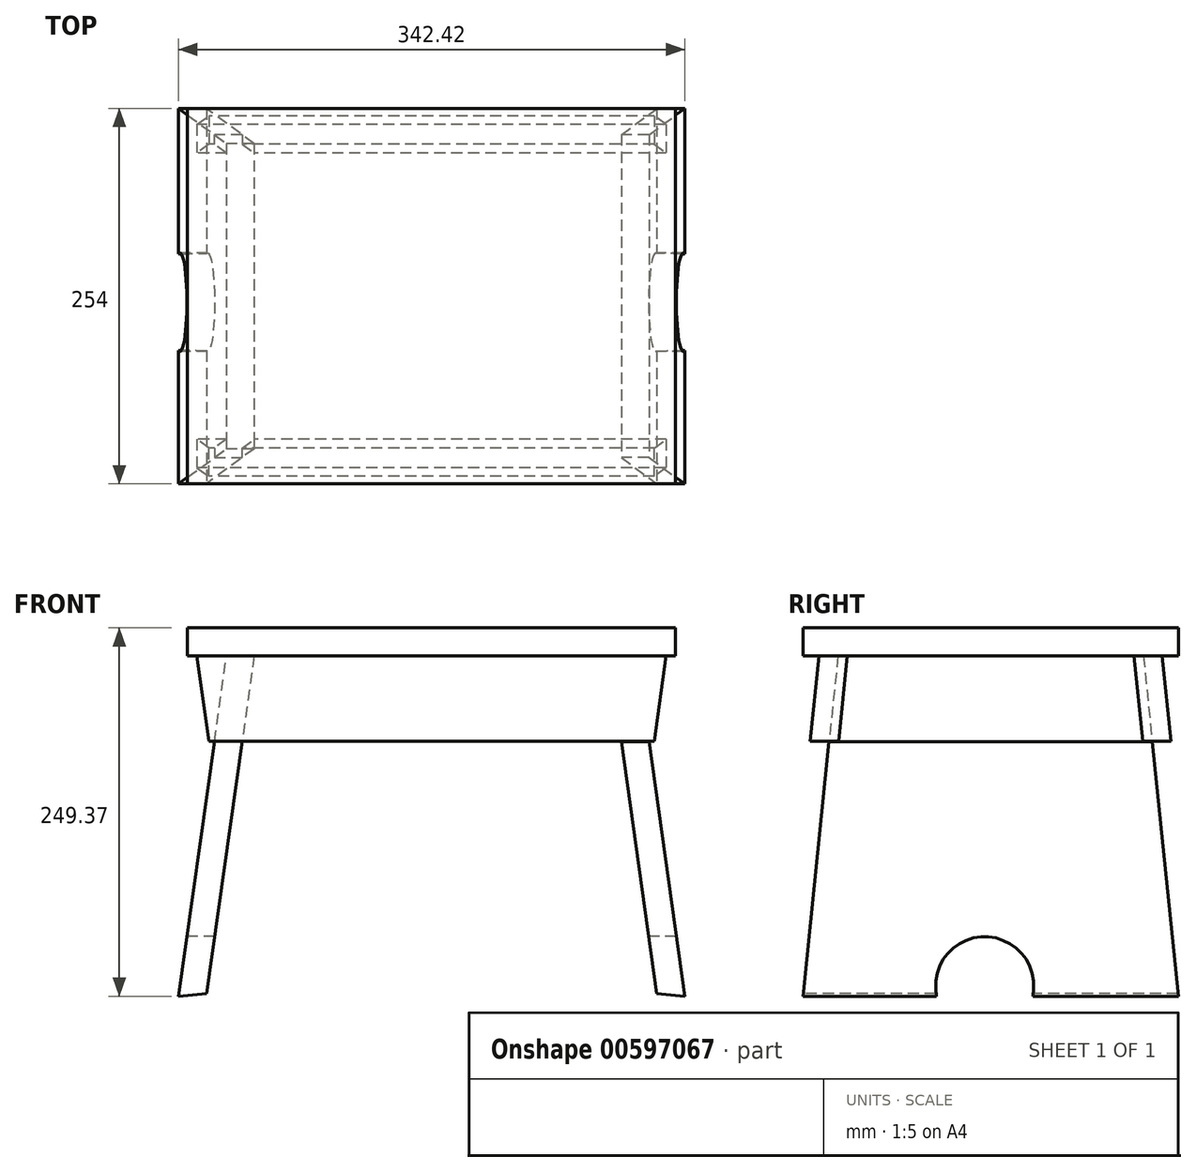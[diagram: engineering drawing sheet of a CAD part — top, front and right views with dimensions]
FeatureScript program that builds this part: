
annotation { "Feature Type Name" : "Feature", "Feature Type Description" : "" }
export const myFeature = defineFeature(function(context is Context, id is Id, definition is map)
    precondition{}
    {
        {
            var Q0;
            Q0=qCreatedBy(makeId("Front.planeOp"),FACE);
            var sketch = newSketch(context, id + "F0", { "sketchPlane" : qUnion([Q0])});
            skLineSegment(sketch, "E0.bottom", {"start": v(165.1, -9.52) * mm, "end": v(-165.1, -9.53) * mm});
            skLineSegment(sketch, "E0.top", {"start": v(165.1, 9.53) * mm, "end": v(-165.1, 9.52) * mm});
            skLineSegment(sketch, "E0.left", {"start": v(165.1, -9.53) * mm, "end": v(165.1, 9.52) * mm});
            skLineSegment(sketch, "E0.right", {"start": v(-165.1, -9.53) * mm, "end": v(-165.1, 9.52) * mm});
            skPoint(sketch, "E0.middle", {"position": v(0, 0) * mm});
            skLineSegment(sketch, "E1.bottom", {"start": v(-165.1, -9.53) * mm, "end": v(165.1, -9.53) * mm, "construction": true});
            skLineSegment(sketch, "E1.top", {"start": v(-165.1, -238.13) * mm, "end": v(165.1, -238.13) * mm, "construction": true});
            skLineSegment(sketch, "E1.left", {"start": v(-165.1, -9.53) * mm, "end": v(-165.1, -238.13) * mm, "construction": true});
            skLineSegment(sketch, "E1.right", {"start": v(165.1, -9.53) * mm, "end": v(165.1, -238.13) * mm, "construction": true});
            skLineSegment(sketch, "E2", {"start": v(171.21, -239.84) * mm, "end": v(152.24, -238.13) * mm});
            skLineSegment(sketch, "E3", {"start": v(0, 0) * mm, "end": v(0, -238.13) * mm, "construction": true});
            skLineSegment(sketch, "E4.MirrorCS", {"start": v(165.1, -9.53) * mm, "end": v(-165.1, -9.53) * mm, "construction": true});
            skLineSegment(sketch, "E5.MirrorCS", {"start": v(-171.21, -239.84) * mm, "end": v(-152.24, -238.13) * mm});
            skLineSegment(sketch, "E6.MirrorCS", {"start": v(-138.85, -9.53) * mm, "end": v(-171.21, -239.84) * mm});
            skLineSegment(sketch, "E7.bottom", {"start": v(-165.1, -9.53) * mm, "end": v(165.1, -9.53) * mm});
            skLineSegment(sketch, "E7.top", {"start": v(-165.1, -67.6) * mm, "end": v(165.1, -67.6) * mm});
            skLineSegment(sketch, "E7.left", {"start": v(-165.1, -9.53) * mm, "end": v(-165.1, -67.6) * mm});
            skLineSegment(sketch, "E7.right", {"start": v(165.1, -9.53) * mm, "end": v(165.1, -67.6) * mm});
            skLineSegment(sketch, "E8", {"start": v(150.59, -67.6) * mm, "end": v(158.75, -9.53) * mm});
            skLineSegment(sketch, "E9.MirrorCS", {"start": v(-150.59, -67.6) * mm, "end": v(-158.75, -9.53) * mm});
            skLineSegment(sketch, "E10", {"start": v(-152.24, -238.13) * mm, "end": v(-120.11, -9.53) * mm});
            skLineSegment(sketch, "E11.MirrorCS", {"start": v(152.24, -238.13) * mm, "end": v(120.11, -9.53) * mm});
            skLineSegment(sketch, "E12.MirrorCS", {"start": v(165.1, -238.13) * mm, "end": v(-165.1, -238.13) * mm, "construction": true});
            skLineSegment(sketch, "E13", {"start": v(171.21, -239.84) * mm, "end": v(138.85, -9.53) * mm});
            skSolve(sketch);
        }
        {
            var Q0;
            Q0=makeQuery(id+"F0.imprint","IMPRINT",FACE,{"disambiguationData":[TD([[makeQuery(id+"F0.imprint","IMPRINT",EDGE,{"derivedFrom":sQuery(id+"F0.wireOp",EDGE,"E0.top")}),1.0]])]});
            extrude(context, id + "F1", {"entities" : qUnion([Q0]), "endBound" : BoundingType.SYMMETRIC, "depth" : 254 * mm, "offsetDistance" : 25.4 * mm});
        }
        {
            var Q0;
            {var subQ0=sQuery(id+"F0.wireOp",EDGE,"E5.MirrorCS");Q0=makeQuery(id+"F0.imprint","IMPRINT",FACE,{"disambiguationData":[TD([[makeQuery(id+"F0.imprint","IMPRINT",EDGE,{"derivedFrom":subQ0}),1.0]])]});}
            var Q1;
            {var subQ0=sQuery(id+"F0.wireOp",EDGE,"E7.bottom");var subQ1=sQuery(id+"F0.wireOp",EDGE,"E6.MirrorCS");var subQ2=makeQuery(id+"F0.imprint","INTERSECT",VERTEX,{"derivedFrom":[subQ1,subQ0]});Q1=makeQuery(id+"F0.imprint","IMPRINT",FACE,{"disambiguationData":[TD([[makeQuery(id+"F0.imprint","IMPRINT",EDGE,{"disambiguationData":[TD([[subQ2,-1.0]])],"derivedFrom":subQ1}),1.0]])]});}
            var Q2;
            {var subQ0=sQuery(id+"F0.wireOp",EDGE,"E11.MirrorCS");var subQ1=sQuery(id+"F0.wireOp",EDGE,"E7.bottom");var subQ2=makeQuery(id+"F0.imprint","INTERSECT",VERTEX,{"derivedFrom":[subQ1,subQ0]});Q2=makeQuery(id+"F0.imprint","IMPRINT",FACE,{"disambiguationData":[TD([[makeQuery(id+"F0.imprint","IMPRINT",EDGE,{"disambiguationData":[TD([[subQ2,-1.0]])],"derivedFrom":subQ1}),-1.0]])]});}
            var Q3;
            {var subQ5=sQuery(id+"F0.wireOp",EDGE,"E2");Q3=makeQuery(id+"F0.imprint","IMPRINT",FACE,{"disambiguationData":[TD([[makeQuery(id+"F0.imprint","IMPRINT",EDGE,{"derivedFrom":subQ5}),-1.0]])]});}
            var Q4;
            Q4=makeQuery(id+"F1.opExtrude","CAP_VERTEX",VERTEX,{"disambiguationData":[OSD([sQuery(id+"F0.wireOp",EDGE,"E0.right"),sQuery(id+"F0.wireOp",EDGE,"E7.bottom"),sQuery(id+"F0.wireOp",EDGE,"E7.left")])],"isStart":true});
            var Q5;
            Q5=makeQuery(id+"F1.opExtrude","CAP_VERTEX",VERTEX,{"disambiguationData":[OSD([sQuery(id+"F0.wireOp",EDGE,"E0.right"),sQuery(id+"F0.wireOp",EDGE,"E7.bottom"),sQuery(id+"F0.wireOp",EDGE,"E7.left")])],"isStart":false});
            extrude(context, id + "F2", {"entities" : qUnion([Q0, Q1, Q2, Q3]), "endBound" : BoundingType.UP_TO_VERTEX, "oppositeDirection" : true, "depth" : 25.4 * mm, "endBoundEntityVertex" : qUnion([Q4]), "offsetDistance" : 25.4 * mm, "hasSecondDirection" : true, "secondDirectionBound" : SecondDirectionBoundingType.UP_TO_VERTEX, "secondDirectionOppositeDirection" : false, "secondDirectionDepth" : 25.4 * mm, "secondDirectionBoundEntityVertex" : qUnion([Q5])});
        }
        {
            var Q0;
            Q0=qCreatedBy(makeId("Right.planeOp"),FACE);
            var sketch = newSketch(context, id + "F3", { "sketchPlane" : qUnion([Q0])});
            skLineSegment(sketch, "E14.0", {"start": v(0, -238.13) * mm, "end": v(0, -9.52) * mm});
            skLineSegment(sketch, "E15.0.0", {"start": v(-127, -239.84) * mm, "end": v(127, -239.84) * mm});
            skLineSegment(sketch, "E15.0.1", {"start": v(127, -239.84) * mm, "end": v(127, -9.52) * mm});
            skLineSegment(sketch, "E15.0.2", {"start": v(127, -9.53) * mm, "end": v(-127, -9.53) * mm});
            skLineSegment(sketch, "E15.0.3", {"start": v(-127, -9.52) * mm, "end": v(-127, -239.84) * mm});
            skLineSegment(sketch, "E16", {"start": v(-127, -239.84) * mm, "end": v(-103.33, -9.53) * mm});
            skLineSegment(sketch, "E17.MirrorCS", {"start": v(127, -9.52) * mm, "end": v(127, -239.84) * mm});
            skLineSegment(sketch, "E18.MirrorCS", {"start": v(127, -239.84) * mm, "end": v(103.33, -9.53) * mm});
            skLineSegment(sketch, "E19", {"start": v(0, -291.04) * mm, "end": v(0, -238.13) * mm, "construction": true});
            skPoint(sketch, "E20", {"position": v(0, -239.84) * mm});
            skArc(sketch, "E21", {"start": v(28.63, -239.84) * mm, "mid": v(-4.06, -199.42) * mm, "end": v(-36.74, -239.84) * mm});
            skSolve(sketch);
        }
        {
            var Q0;
            {var subQ0=sQuery(id+"F3.wireOp",EDGE,"E15.0.3");Q0=makeQuery(id+"F3.imprint","IMPRINT",FACE,{"disambiguationData":[TD([[makeQuery(id+"F3.imprint","IMPRINT",EDGE,{"derivedFrom":subQ0}),1.0]])]});}
            var Q1;
            {var subQ2=sQuery(id+"F3.wireOp",EDGE,"E18.MirrorCS");Q1=makeQuery(id+"F3.imprint","IMPRINT",FACE,{"disambiguationData":[TD([[makeQuery(id+"F3.imprint","IMPRINT",EDGE,{"derivedFrom":subQ2}),-1.0]])]});}
            var Q2;
            {var subQ0=sQuery(id+"F3.wireOp",EDGE,"9yOnda90-AFQG-UzKH-hqDP-Q9mGtrejbege");var subQ1=sQuery(id+"F3.wireOp",EDGE,"E15.0.0");var subQ2=makeQuery(id+"F3.imprint","INTERSECT",VERTEX,{"disambiguationData":[OD(0.0)],"derivedFrom":[subQ1,subQ0]});Q2=makeQuery(id+"F3.imprint","IMPRINT",FACE,{"disambiguationData":[TD([[makeQuery(id+"F3.imprint","IMPRINT",EDGE,{"disambiguationData":[TD([[subQ2,1.0]])],"derivedFrom":subQ1}),1.0]])]});}
            extrude(context, id + "F4", {"entities" : qUnion([Q0, Q1, Q2]), "operationType" : NewBodyOperationType.REMOVE, "endBound" : BoundingType.THROUGH_ALL, "depth" : 25.4 * mm, "offsetDistance" : 25.4 * mm, "hasSecondDirection" : true, "secondDirectionBound" : SecondDirectionBoundingType.THROUGH_ALL, "secondDirectionOppositeDirection" : true, "secondDirectionDepth" : 25.4 * mm});
        }
        {
            var Q0;
            {var subQ0=sQuery(id+"F0.wireOp",EDGE,"E7.right");Q0=makeQuery(id+"F0.imprint","IMPRINT",FACE,{"disambiguationData":[TD([[makeQuery(id+"F0.imprint","IMPRINT",EDGE,{"derivedFrom":subQ0}),-1.0]])]});}
            var Q1;
            {var subQ0=sQuery(id+"F0.wireOp",EDGE,"E7.left");Q1=makeQuery(id+"F0.imprint","IMPRINT",FACE,{"disambiguationData":[TD([[makeQuery(id+"F0.imprint","IMPRINT",EDGE,{"derivedFrom":subQ0}),1.0]])]});}
            extrude(context, id + "F5", {"entities" : qUnion([Q0, Q1]), "operationType" : NewBodyOperationType.REMOVE, "endBound" : BoundingType.THROUGH_ALL, "oppositeDirection" : true, "depth" : 25.4 * mm, "offsetDistance" : 25.4 * mm, "hasSecondDirection" : true, "secondDirectionBound" : SecondDirectionBoundingType.THROUGH_ALL, "secondDirectionOppositeDirection" : false, "secondDirectionDepth" : 25.4 * mm});
        }
        {
            var Q0;
            Q0=qCreatedBy(makeId("Right.planeOp"),FACE);
            var sketch = newSketch(context, id + "F6", { "sketchPlane" : qUnion([Q0])});
            skLineSegment(sketch, "E22.0", {"start": v(-103.33, -9.52) * mm, "end": v(-126.82, -238.12) * mm});
            skLineSegment(sketch, "E23.0", {"start": v(-127, -9.53) * mm, "end": v(127, -9.53) * mm});
            skLineSegment(sketch, "E24.0", {"start": v(103.33, -9.53) * mm, "end": v(126.82, -238.13) * mm});
            skLineSegment(sketch, "E25", {"start": v(-116.1, -9.53) * mm, "end": v(-122.03, -67.22) * mm});
            skLineSegment(sketch, "E26", {"start": v(-122.03, -67.22) * mm, "end": v(-102.88, -67.22) * mm});
            skLineSegment(sketch, "E27", {"start": v(-102.88, -67.22) * mm, "end": v(-96.95, -9.53) * mm});
            skLineSegment(sketch, "E28", {"start": v(-96.95, -9.53) * mm, "end": v(-116.1, -9.53) * mm});
            skLineSegment(sketch, "E29", {"start": v(0, -67.22) * mm, "end": v(-102.88, -67.22) * mm});
            skLineSegment(sketch, "E30.MirrorCS", {"start": v(116.1, -9.53) * mm, "end": v(122.03, -67.22) * mm});
            skLineSegment(sketch, "E31.MirrorCS", {"start": v(96.95, -9.53) * mm, "end": v(116.1, -9.53) * mm});
            skLineSegment(sketch, "E32.MirrorCS", {"start": v(102.88, -67.22) * mm, "end": v(96.95, -9.53) * mm});
            skLineSegment(sketch, "E33.MirrorCS", {"start": v(122.03, -67.22) * mm, "end": v(102.88, -67.22) * mm});
            skSolve(sketch);
        }
        {
            var Q0;
            {var subQ5=sQuery(id+"F6.wireOp",EDGE,"E25");Q0=makeQuery(id+"F6.imprint","IMPRINT",FACE,{"disambiguationData":[TD([[makeQuery(id+"F6.imprint","IMPRINT",EDGE,{"derivedFrom":subQ5}),1.0]])]});}
            var Q1;
            {var subQ5=sQuery(id+"F6.wireOp",EDGE,"E27");Q1=makeQuery(id+"F6.imprint","IMPRINT",FACE,{"disambiguationData":[TD([[makeQuery(id+"F6.imprint","IMPRINT",EDGE,{"derivedFrom":subQ5}),1.0]])]});}
            var Q2;
            {var subQ5=sQuery(id+"F6.wireOp",EDGE,"E30.MirrorCS");Q2=makeQuery(id+"F6.imprint","IMPRINT",FACE,{"disambiguationData":[TD([[makeQuery(id+"F6.imprint","IMPRINT",EDGE,{"derivedFrom":subQ5}),-1.0]])]});}
            var Q3;
            {var subQ5=sQuery(id+"F6.wireOp",EDGE,"E32.MirrorCS");Q3=makeQuery(id+"F6.imprint","IMPRINT",FACE,{"disambiguationData":[TD([[makeQuery(id+"F6.imprint","IMPRINT",EDGE,{"derivedFrom":subQ5}),-1.0]])]});}
            var Q4;
            Q4=makeQuery(id+"F1.opExtrude","SWEPT_FACE",FACE,{"disambiguationData":[OSD([sQuery(id+"F0.wireOp",EDGE,"E0.left")])]});
            var Q5;
            Q5=makeQuery(id+"F1.opExtrude","SWEPT_FACE",FACE,{"disambiguationData":[OSD([sQuery(id+"F0.wireOp",EDGE,"E0.right")])]});
            extrude(context, id + "F7", {"entities" : qUnion([Q0, Q1, Q2, Q3]), "endBound" : BoundingType.UP_TO_SURFACE, "depth" : 25.4 * mm, "endBoundEntityFace" : qUnion([Q4]), "offsetDistance" : 25.4 * mm, "hasSecondDirection" : true, "secondDirectionBound" : SecondDirectionBoundingType.UP_TO_SURFACE, "secondDirectionOppositeDirection" : true, "secondDirectionDepth" : 25.4 * mm, "secondDirectionBoundEntityFace" : qUnion([Q5])});
        }
        {
            var Q0;
            {var subQ0=sQuery(id+"F0.wireOp",EDGE,"E7.right");Q0=makeQuery(id+"F0.imprint","IMPRINT",FACE,{"disambiguationData":[TD([[makeQuery(id+"F0.imprint","IMPRINT",EDGE,{"derivedFrom":subQ0}),-1.0]])]});}
            var Q1;
            {var subQ0=sQuery(id+"F0.wireOp",EDGE,"E7.left");Q1=makeQuery(id+"F0.imprint","IMPRINT",FACE,{"disambiguationData":[TD([[makeQuery(id+"F0.imprint","IMPRINT",EDGE,{"derivedFrom":subQ0}),1.0]])]});}
            extrude(context, id + "F8", {"entities" : qUnion([Q0, Q1]), "operationType" : NewBodyOperationType.REMOVE, "endBound" : BoundingType.THROUGH_ALL, "oppositeDirection" : true, "depth" : 25.4 * mm, "offsetDistance" : 25.4 * mm, "hasSecondDirection" : true, "secondDirectionBound" : SecondDirectionBoundingType.THROUGH_ALL, "secondDirectionOppositeDirection" : false, "secondDirectionDepth" : 25.4 * mm});
        }
        {
            var Q0;
            Q0=makeQuery(id+"F2.opExtrude","SWEPT_BODY",BODY,{"disambiguationData":[OSD([sQuery(id+"F0.wireOp",EDGE,"E7.bottom"),sQuery(id+"F0.wireOp",EDGE,"E2"),sQuery(id+"F0.wireOp",EDGE,"E11.MirrorCS"),sQuery(id+"F0.wireOp",EDGE,"E13")])]});
            var Q1;
            Q1=makeQuery(id+"F7.opExtrude","SWEPT_BODY",BODY,{"disambiguationData":[OSD([sQuery(id+"F6.wireOp",EDGE,"E25"),sQuery(id+"F6.wireOp",EDGE,"E26"),sQuery(id+"F6.wireOp",EDGE,"E27"),sQuery(id+"F6.wireOp",EDGE,"E28")])]});
            booleanBodies(context, id + "F9", {"operationType" : BooleanOperationType.SUBTRACTION, "tools" : qUnion([Q0]), "targets" : qUnion([Q1]), "keepTools" : true});
        }
        {
            var Q0;
            Q0=makeQuery(id+"F2.opExtrude","SWEPT_BODY",BODY,{"disambiguationData":[OSD([sQuery(id+"F0.wireOp",EDGE,"E7.bottom"),sQuery(id+"F0.wireOp",EDGE,"E2"),sQuery(id+"F0.wireOp",EDGE,"E11.MirrorCS"),sQuery(id+"F0.wireOp",EDGE,"E13")])]});
            var Q1;
            Q1=makeQuery(id+"F7.opExtrude","SWEPT_BODY",BODY,{"disambiguationData":[OSD([sQuery(id+"F6.wireOp",EDGE,"E30.MirrorCS"),sQuery(id+"F6.wireOp",EDGE,"E31.MirrorCS"),sQuery(id+"F6.wireOp",EDGE,"E32.MirrorCS"),sQuery(id+"F6.wireOp",EDGE,"E33.MirrorCS")])]});
            booleanBodies(context, id + "F10", {"operationType" : BooleanOperationType.SUBTRACTION, "tools" : qUnion([Q0]), "targets" : qUnion([Q1]), "keepTools" : true});
        }
        {
            var Q0;
            Q0=makeQuery(id+"F2.opExtrude","SWEPT_BODY",BODY,{"disambiguationData":[OSD([sQuery(id+"F0.wireOp",EDGE,"E5.MirrorCS"),sQuery(id+"F0.wireOp",EDGE,"E6.MirrorCS"),sQuery(id+"F0.wireOp",EDGE,"E7.bottom"),sQuery(id+"F0.wireOp",EDGE,"E10")])]});
            var Q1;
            Q1=makeQuery(id+"F7.opExtrude","SWEPT_BODY",BODY,{"disambiguationData":[OSD([sQuery(id+"F6.wireOp",EDGE,"E30.MirrorCS"),sQuery(id+"F6.wireOp",EDGE,"E31.MirrorCS"),sQuery(id+"F6.wireOp",EDGE,"E32.MirrorCS"),sQuery(id+"F6.wireOp",EDGE,"E33.MirrorCS")])]});
            booleanBodies(context, id + "F11", {"operationType" : BooleanOperationType.SUBTRACTION, "tools" : qUnion([Q0]), "targets" : qUnion([Q1]), "keepTools" : true});
        }
        {
            var Q0;
            Q0=makeQuery(id+"F2.opExtrude","SWEPT_BODY",BODY,{"disambiguationData":[OSD([sQuery(id+"F0.wireOp",EDGE,"E5.MirrorCS"),sQuery(id+"F0.wireOp",EDGE,"E6.MirrorCS"),sQuery(id+"F0.wireOp",EDGE,"E7.bottom"),sQuery(id+"F0.wireOp",EDGE,"E10")])]});
            var Q1;
            Q1=makeQuery(id+"F7.opExtrude","SWEPT_BODY",BODY,{"disambiguationData":[OSD([sQuery(id+"F6.wireOp",EDGE,"E25"),sQuery(id+"F6.wireOp",EDGE,"E26"),sQuery(id+"F6.wireOp",EDGE,"E27"),sQuery(id+"F6.wireOp",EDGE,"E28")])]});
            booleanBodies(context, id + "F12", {"operationType" : BooleanOperationType.SUBTRACTION, "tools" : qUnion([Q0]), "targets" : qUnion([Q1]), "keepTools" : true});
        }
    });
